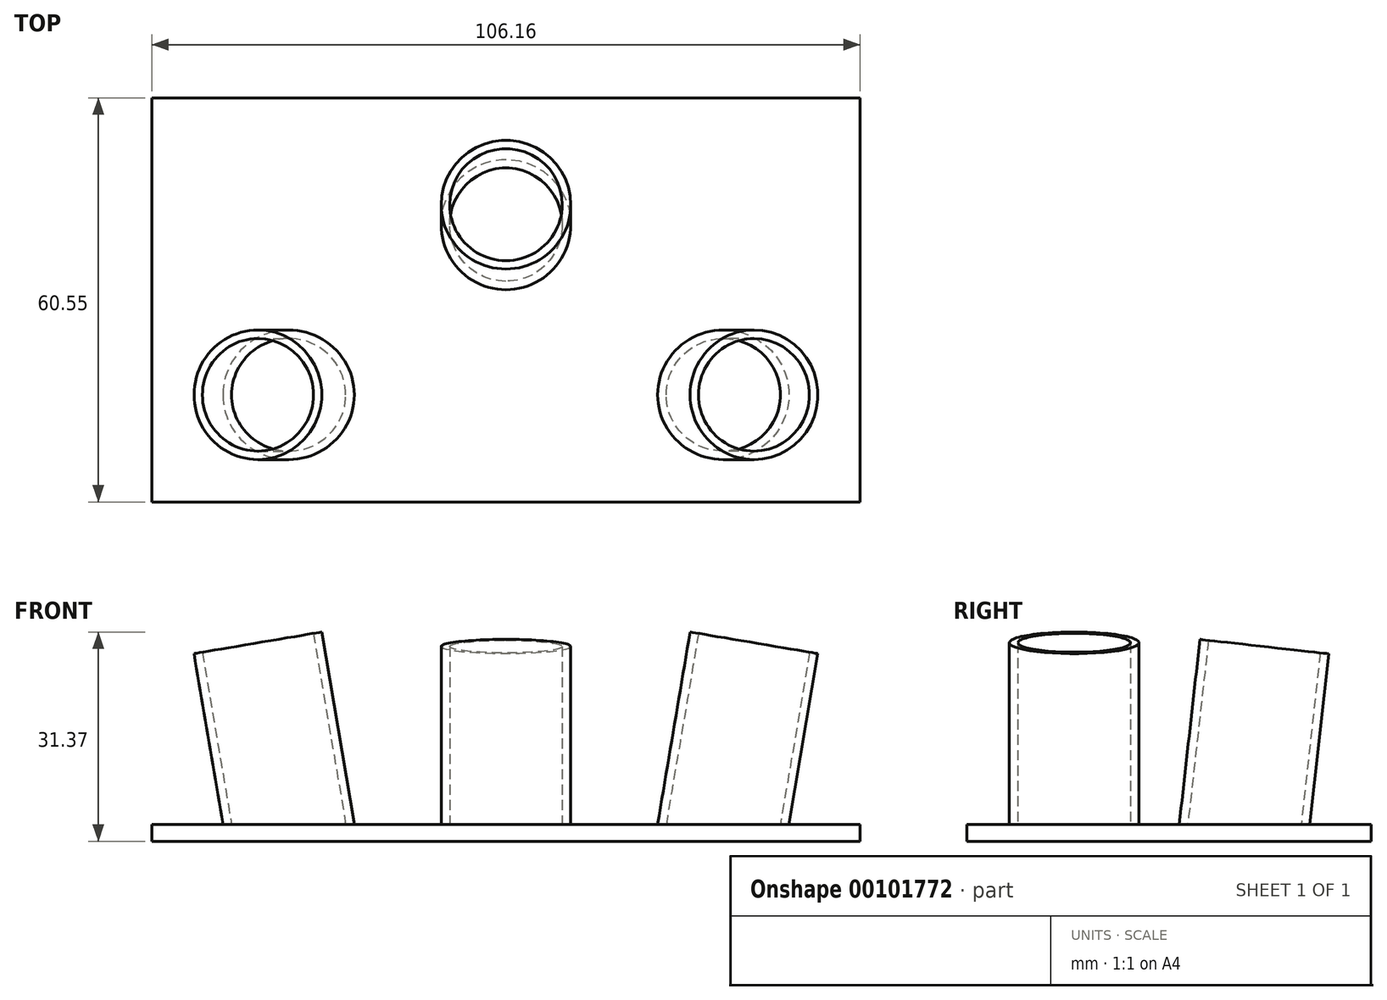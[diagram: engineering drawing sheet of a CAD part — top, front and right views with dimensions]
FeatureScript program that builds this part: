
annotation { "Feature Type Name" : "Feature", "Feature Type Description" : "" }
export const myFeature = defineFeature(function(context is Context, id is Id, definition is map)
    precondition{}
    {
        {
            var Q0;
            Q0=qCreatedBy(makeId("Top.planeOp"),FACE);
            var sketch = newSketch(context, id + "F0", { "sketchPlane" : qUnion([Q0])});
            skLineSegment(sketch, "E0", {"start": v(0, 76.47) * mm, "end": v(0, -74.5) * mm, "construction": true});
            skSolve(sketch);
        }
        {
            var Q0;
            Q0=sQuery(id+"F0.wireOp",EDGE,"E0");
            cPlane(context, id + "F1", {"entities" : qUnion([Q0]), "cplaneType" : CPlaneType.LINE_ANGLE, "offset" : 152.4 * mm, "angle" : 9.6 * degree, "width" : 152.4 * mm, "height" : 152.4 * mm});
        }
        {
            var Q0;
            Q0=qCreatedBy(id+"F1.planeOp",FACE);
            var sketch = newSketch(context, id + "F2", { "sketchPlane" : qUnion([Q0])});
            skCircle(sketch, "E1", {"center": v(-32.11, 38.14) * mm, "radius": 8.44 * mm});
            skCircle(sketch, "E2", {"center": v(-32.11, 38.14) * mm, "radius": 9.7 * mm});
            skSolve(sketch);
        }
        {
            var Q0;
            Q0 = qSketchRegion(id + "F2", true);
            extrude(context, id + "F3", {"entities" : qUnion([Q0]), "oppositeDirection" : true, "depth" : 33.02 * mm});
        }
        {
            var Q0;
            Q0=makeQuery(id+"F3.opExtrude","CAP_FACE",FACE,{"disambiguationData":[OSD([sQuery(id+"F2.wireOp",EDGE,"E1"),sQuery(id+"F2.wireOp",EDGE,"E2")])],"isStart":false});
            extrude(context, id + "F4", {"entities" : qUnion([Q0]), "operationType" : NewBodyOperationType.ADD, "oppositeDirection" : true, "depth" : 50.8 * mm});
        }
        {
            var Q0;
            Q0=qCreatedBy(makeId("Front.planeOp"),FACE);
            var sketch = newSketch(context, id + "F5", { "sketchPlane" : qUnion([Q0])});
            skLineSegment(sketch, "E3.bottom", {"start": v(0, 0) * mm, "end": v(43.35, 0) * mm});
            skLineSegment(sketch, "E3.top", {"start": v(-49.4, -35.3) * mm, "end": v(43.35, -35.3) * mm});
            skLineSegment(sketch, "E3.left", {"start": v(-49.4, 0) * mm, "end": v(-49.4, -35.3) * mm});
            skLineSegment(sketch, "E3.right", {"start": v(43.35, 0) * mm, "end": v(43.35, -35.3) * mm});
            skLineSegment(sketch, "E4", {"start": v(-49.4, 0) * mm, "end": v(0, 0) * mm});
            skSolve(sketch);
        }
        {
            var Q0;
            Q0=makeQuery(id+"F5.imprint","IMPRINT",FACE,{"disambiguationData":[TD([[makeQuery(id+"F5.imprint","IMPRINT",EDGE,{"derivedFrom":sQuery(id+"F5.wireOp",EDGE,"E3.bottom")}),-1.0]])]});
            extrude(context, id + "F6", {"entities" : qUnion([Q0]), "operationType" : NewBodyOperationType.REMOVE, "endBound" : BoundingType.SYMMETRIC, "depth" : 254 * mm});
        }
        {
            var Q0;
            Q0=sQuery(id+"F0.wireOp",EDGE,"E0");
            cPlane(context, id + "F7", {"entities" : qUnion([Q0]), "cplaneType" : CPlaneType.LINE_ANGLE, "offset" : 152.4 * mm, "angle" : 350.41 * degree, "width" : 152.4 * mm, "height" : 152.4 * mm});
        }
        {
            var Q0;
            Q0=qCreatedBy(id+"F7.planeOp",FACE);
            var sketch = newSketch(context, id + "F8", { "sketchPlane" : qUnion([Q0])});
            skCircle(sketch, "E5", {"center": v(32.11, 38.14) * mm, "radius": 8.44 * mm});
            skCircle(sketch, "E6", {"center": v(32.11, 38.14) * mm, "radius": 9.7 * mm});
            skLineSegment(sketch, "E7", {"start": v(-41.82, -67.55) * mm, "end": v(-41.82, 69.02) * mm, "construction": true});
            skSolve(sketch);
        }
        {
            var Q0;
            Q0 = qSketchRegion(id + "F8", true);
            extrude(context, id + "F9", {"entities" : qUnion([Q0]), "oppositeDirection" : true, "depth" : 33.02 * mm});
        }
        {
            var Q0;
            Q0=qCreatedBy(makeId("Front.planeOp"),FACE);
            var sketch = newSketch(context, id + "F10", { "sketchPlane" : qUnion([Q0])});
            skLineSegment(sketch, "E8.bottom", {"start": v(-69.48, 0) * mm, "end": v(74.8, 0) * mm});
            skLineSegment(sketch, "E8.top", {"start": v(-69.48, -44) * mm, "end": v(74.8, -44) * mm});
            skLineSegment(sketch, "E8.left", {"start": v(-69.48, 0) * mm, "end": v(-69.48, -44) * mm});
            skLineSegment(sketch, "E8.right", {"start": v(74.8, 0) * mm, "end": v(74.8, -44) * mm});
            skSolve(sketch);
        }
        {
            var Q0;
            Q0 = qSketchRegion(id + "F10", true);
            extrude(context, id + "F11", {"entities" : qUnion([Q0]), "operationType" : NewBodyOperationType.REMOVE, "endBound" : BoundingType.SYMMETRIC, "oppositeDirection" : true, "depth" : 762 * mm});
        }
        {
            var Q0;
            Q0=qCreatedBy(makeId("Top.planeOp"),FACE);
            var sketch = newSketch(context, id + "F12", { "sketchPlane" : qUnion([Q0])});
            skLineSegment(sketch, "E9", {"start": v(-73.7, 0) * mm, "end": v(71.32, 0) * mm, "construction": true});
            skSolve(sketch);
        }
        {
            var Q0;
            Q0 = qBodyType(qCreatedBy(id + "F12" ,EDGE), BodyType.WIRE);
            cPlane(context, id + "F13", {"entities" : qUnion([Q0]), "cplaneType" : CPlaneType.LINE_ANGLE, "offset" : 152.4 * mm, "angle" : 83.6 * degree, "width" : 152.4 * mm, "height" : 152.4 * mm});
        }
        {
            var Q0;
            Q0=qCreatedBy(id+"F13.planeOp",FACE);
            var sketch = newSketch(context, id + "F14", { "sketchPlane" : qUnion([Q0])});
            skCircle(sketch, "E10", {"center": v(0, -12.55) * mm, "radius": 8.44 * mm});
            skCircle(sketch, "E11", {"center": v(0, -12.55) * mm, "radius": 9.7 * mm});
            skSolve(sketch);
        }
        {
            var Q0;
            Q0 = qSketchRegion(id + "F14", true);
            extrude(context, id + "F15", {"entities" : qUnion([Q0]), "depth" : 25.4 * mm});
        }
        {
            var Q0;
            Q0=makeQuery(id+"F15.opExtrude","CAP_FACE",FACE,{"disambiguationData":[OSD([sQuery(id+"F14.wireOp",EDGE,"E10"),sQuery(id+"F14.wireOp",EDGE,"E11")])],"isStart":false});
            extrude(context, id + "F16", {"entities" : qUnion([Q0]), "operationType" : NewBodyOperationType.ADD, "oppositeDirection" : true, "depth" : 50.8 * mm});
        }
        {
            var Q0;
            Q0=qCreatedBy(makeId("Right.planeOp"),FACE);
            var sketch = newSketch(context, id + "F17", { "sketchPlane" : qUnion([Q0])});
            skLineSegment(sketch, "E12.bottom", {"start": v(-65.01, 0) * mm, "end": v(29.18, 0) * mm});
            skLineSegment(sketch, "E12.top", {"start": v(-65.01, -29.38) * mm, "end": v(29.18, -29.38) * mm});
            skLineSegment(sketch, "E12.left", {"start": v(-65.01, 0) * mm, "end": v(-65.01, -29.38) * mm});
            skLineSegment(sketch, "E12.right", {"start": v(29.18, 0) * mm, "end": v(29.18, -29.38) * mm});
            skSolve(sketch);
        }
        {
            var Q0;
            Q0 = qSketchRegion(id + "F17", true);
            extrude(context, id + "F18", {"entities" : qUnion([Q0]), "operationType" : NewBodyOperationType.REMOVE, "endBound" : BoundingType.SYMMETRIC, "oppositeDirection" : true, "depth" : 254 * mm});
        }
        {
            var Q0;
            Q0=qCreatedBy(makeId("Top.planeOp"),FACE);
            var sketch = newSketch(context, id + "F19", { "sketchPlane" : qUnion([Q0])});
            skLineSegment(sketch, "E13.bottom", {"start": v(-53.08, -54.2) * mm, "end": v(53.08, -54.2) * mm});
            skLineSegment(sketch, "E13.top", {"start": v(-53.08, 6.35) * mm, "end": v(53.08, 6.35) * mm});
            skLineSegment(sketch, "E13.left", {"start": v(-53.08, -54.2) * mm, "end": v(-53.08, 6.35) * mm});
            skLineSegment(sketch, "E13.right", {"start": v(53.08, -54.2) * mm, "end": v(53.08, 6.35) * mm});
            skLineSegment(sketch, "E14", {"start": v(-46.73, -71.54) * mm, "end": v(-46.73, 70.82) * mm, "construction": true});
            skLineSegment(sketch, "E15", {"start": v(46.73, -72.33) * mm, "end": v(46.73, 72.4) * mm, "construction": true});
            skLineSegment(sketch, "E16", {"start": v(-71.07, -47.85) * mm, "end": v(71.5, -47.85) * mm, "construction": true});
            skSolve(sketch);
        }
        {
            var Q0;
            Q0 = qSketchRegion(id + "F19", true);
            extrude(context, id + "F20", {"entities" : qUnion([Q0]), "operationType" : NewBodyOperationType.ADD, "oppositeDirection" : true, "depth" : 2.54 * mm});
        }
    });
